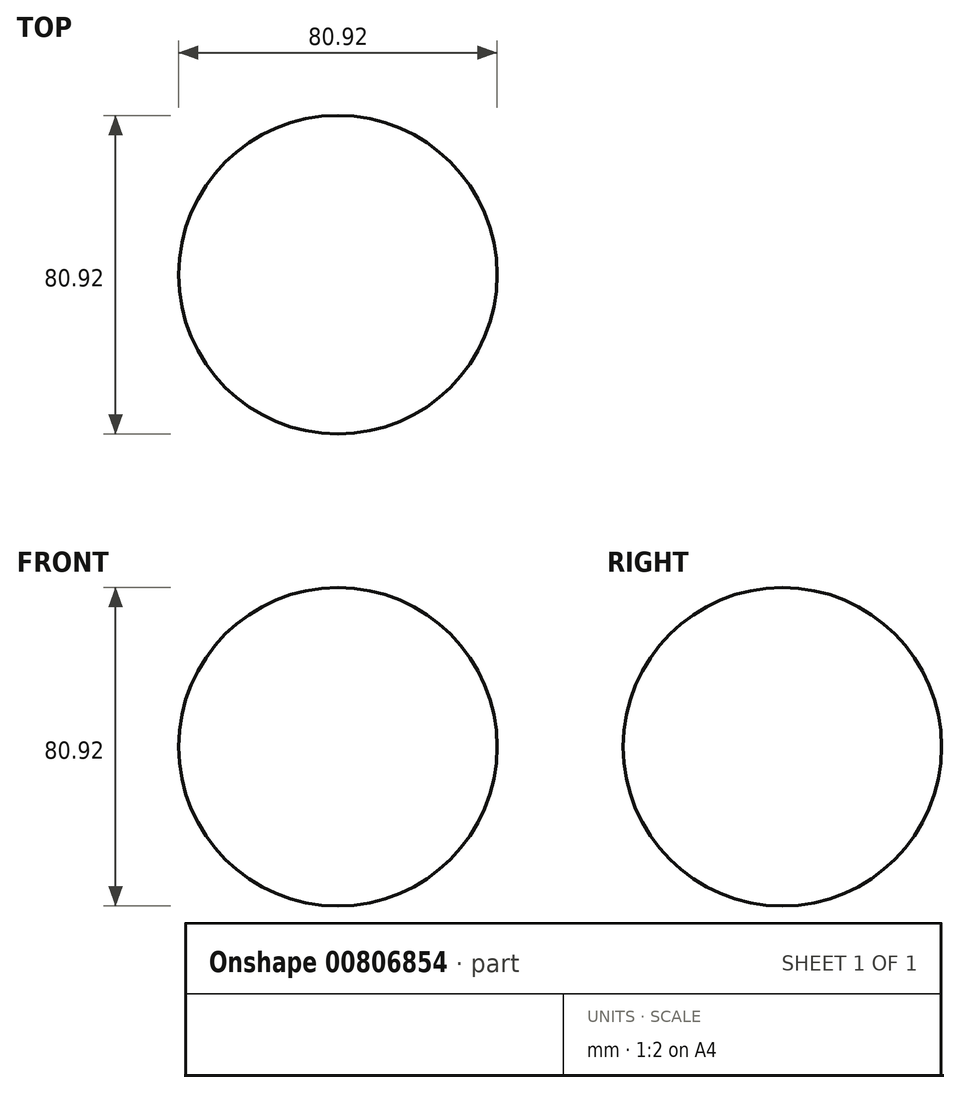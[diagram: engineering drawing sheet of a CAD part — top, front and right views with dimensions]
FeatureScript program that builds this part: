
annotation { "Feature Type Name" : "Feature", "Feature Type Description" : "" }
export const myFeature = defineFeature(function(context is Context, id is Id, definition is map)
    precondition{}
    {
        {
            var Q0;
            Q0=qCreatedBy(makeId("Front.planeOp"),FACE);
            var sketch = newSketch(context, id + "F0", { "sketchPlane" : qUnion([Q0])});
            skCircle(sketch, "E0", {"center": v(0, 0) * mm, "radius": 40.46 * mm});
            skLineSegment(sketch, "E1", {"start": v(0, 53.21) * mm, "end": v(0, -67.6) * mm});
            skSolve(sketch);
        }
        {
            var Q0;
            {var subQ0=sQuery(id+"F0.wireOp",EDGE,"E1");var subQ1=sQuery(id+"F0.wireOp",EDGE,"E0");var subQ2=makeQuery(id+"F0.imprint","INTERSECT",VERTEX,{"disambiguationData":[OD(0.0)],"derivedFrom":[subQ1,subQ0]});Q0=makeQuery(id+"F0.imprint","IMPRINT",FACE,{"disambiguationData":[TD([[makeQuery(id+"F0.imprint","IMPRINT",EDGE,{"disambiguationData":[TD([[subQ2,1.0]])],"derivedFrom":subQ1}),1.0]])]});}
            var Q1;
            Q1=sQuery(id+"F0.wireOp",EDGE,"E1");
            revolve(context, id + "F1", {"surfaceOperationType" : NewSurfaceOperationType.NEW, "entities" : qUnion([Q0]), "axis" : qUnion([Q1]), "revolveType" : RevolveType.FULL});
        }
    });
